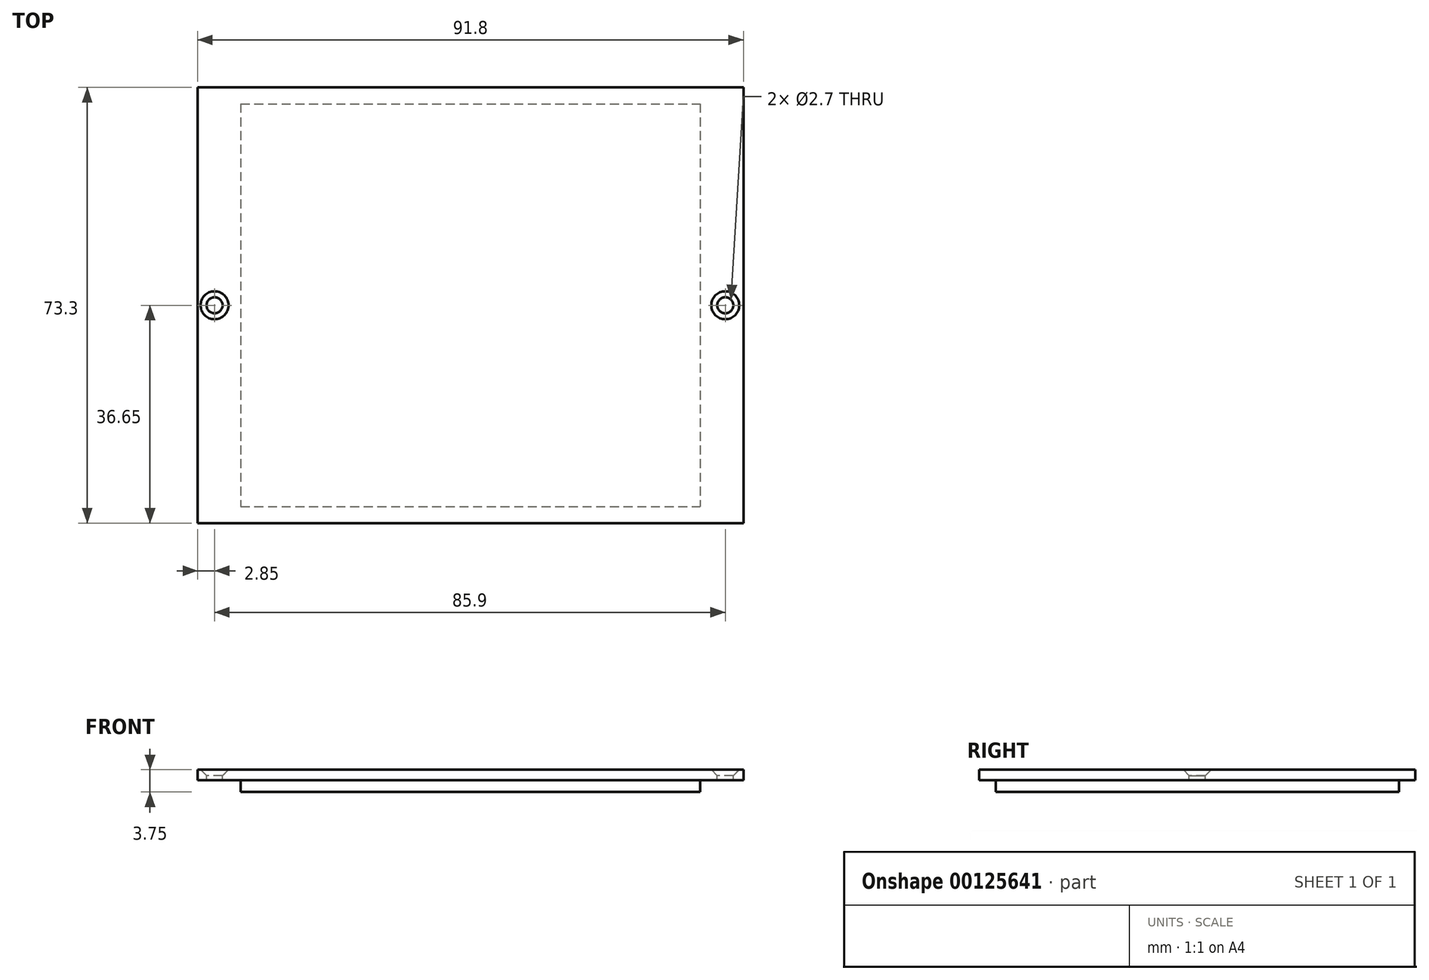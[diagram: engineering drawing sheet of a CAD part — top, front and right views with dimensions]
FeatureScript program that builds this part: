
annotation { "Feature Type Name" : "Feature", "Feature Type Description" : "" }
export const myFeature = defineFeature(function(context is Context, id is Id, definition is map)
    precondition{}
    {
        {
            var Q0;
            Q0=qCreatedBy(makeId("Top.planeOp"),FACE);
            var sketch = newSketch(context, id + "F0", { "sketchPlane" : qUnion([Q0])});
            skLineSegment(sketch, "E0.bottom", {"start": v(-39.75, 32.65) * mm, "end": v(37.55, 32.65) * mm});
            skLineSegment(sketch, "E0.top", {"start": v(-39.75, -35.15) * mm, "end": v(37.55, -35.15) * mm});
            skLineSegment(sketch, "E0.left", {"start": v(-39.75, 32.65) * mm, "end": v(-39.75, -35.15) * mm});
            skLineSegment(sketch, "E0.right", {"start": v(37.55, 32.65) * mm, "end": v(37.55, -35.15) * mm});
            skLineSegment(sketch, "E1.bottom", {"start": v(44.8, -37.9) * mm, "end": v(-47, -37.9) * mm});
            skLineSegment(sketch, "E1.top", {"start": v(44.8, 35.4) * mm, "end": v(-47, 35.4) * mm});
            skLineSegment(sketch, "E1.left", {"start": v(44.8, -37.9) * mm, "end": v(44.8, 35.4) * mm});
            skLineSegment(sketch, "E1.right", {"start": v(-47, -37.9) * mm, "end": v(-47, 35.4) * mm});
            skPoint(sketch, "E2", {"position": v(-44.15, -1.25) * mm});
            skPoint(sketch, "E3", {"position": v(41.75, -1.25) * mm});
            skSolve(sketch);
        }
        {
            var Q0;
            Q0=qSketchRegion(id+"F0",true);
            extrude(context, id + "F1", {"entities" : qUnion([Q0]), "oppositeDirection" : true, "depth" : 1.75 * mm});
        }
        {
            var Q0;
            Q0=makeQuery(id+"F0.imprint","IMPRINT",FACE,{"disambiguationData":[TD([[makeQuery(id+"F0.imprint","IMPRINT",EDGE,{"derivedFrom":sQuery(id+"F0.wireOp",EDGE,"E0.bottom")}),-1.0]])]});
            extrude(context, id + "F2", {"entities" : qUnion([Q0]), "operationType" : NewBodyOperationType.ADD, "oppositeDirection" : true, "depth" : 3.75 * mm});
        }
        {
            var Q0;
            Q0=sQuery(id+"F0.wireOp",VERTEX,"E2");
            var Q1;
            Q1=sQuery(id+"F0.wireOp",VERTEX,"E3");
            var Q2;
            Q2=makeQuery(id+"F1.opExtrude","SWEPT_BODY",BODY,{"disambiguationData":[OSD([sQuery(id+"F0.wireOp",EDGE,"E0.bottom"),sQuery(id+"F0.wireOp",EDGE,"E0.top"),sQuery(id+"F0.wireOp",EDGE,"E0.left"),sQuery(id+"F0.wireOp",EDGE,"E0.right"),sQuery(id+"F0.wireOp",EDGE,"E1.bottom"),sQuery(id+"F0.wireOp",EDGE,"E1.top"),sQuery(id+"F0.wireOp",EDGE,"E1.left"),sQuery(id+"F0.wireOp",EDGE,"E1.right")])]});
            hole(context, id + "F3", {"style" : HoleStyle.C_SINK, "endStyle" : HoleEndStyle.THROUGH, "holeDiameter" : 2.7 * mm, "cSinkDiameter" : 4.7 * mm, "cSinkAngle" : 90 * degree, "startFromSketch" : true, "locations" : qUnion([Q0, Q1]), "scope" : qUnion([Q2]), "isTappedThrough" : true});
        }
    });
